SOLIDWORKS PART (.sldprt)
format: sldprt  version: not decoded by parser v0  size: 277,504 bytes
history: native  units: mm
features: sketch x2, fillet x2, extrude x1, cut_extrude x1, chamfer x1 (+10 scaffold rows collapsed)
feature tree (17):
  scaffold x10  (default folders/planes/origin — collapsed)
  sketch  "Sketch1"  dims[D1=3.5mm]
  extrude  "Extrude1"  Depth=1.651mm
  fillet  "Fillet1"  Radius=0.6mm
  sketch  "Sketch2"  dims[c1.D1=2.159mm c1.D2=~1.49394mm c2.D1=1.25mm c2.D2=2.5mm c2.D3=1.25mm c2.D4=2.5mm c2.D5=0.5mm c2.D6=0.25mm c2.D7=0.25mm c2.D8=0.5mm]
  cut_extrude  "Cut-Extrude2"  Depth=0.35mm
  chamfer  "Chamfer1"  Distance=0.2mm Angle=45deg
  fillet  "Fillet2"  Radius=0.35mm
decode coverage: 7 of 7 modeling features carry decoded parameters
note: ~ marks probable driven/reference dimensions
note: suppression state not decoded; provenance and decode notes live in map.json
